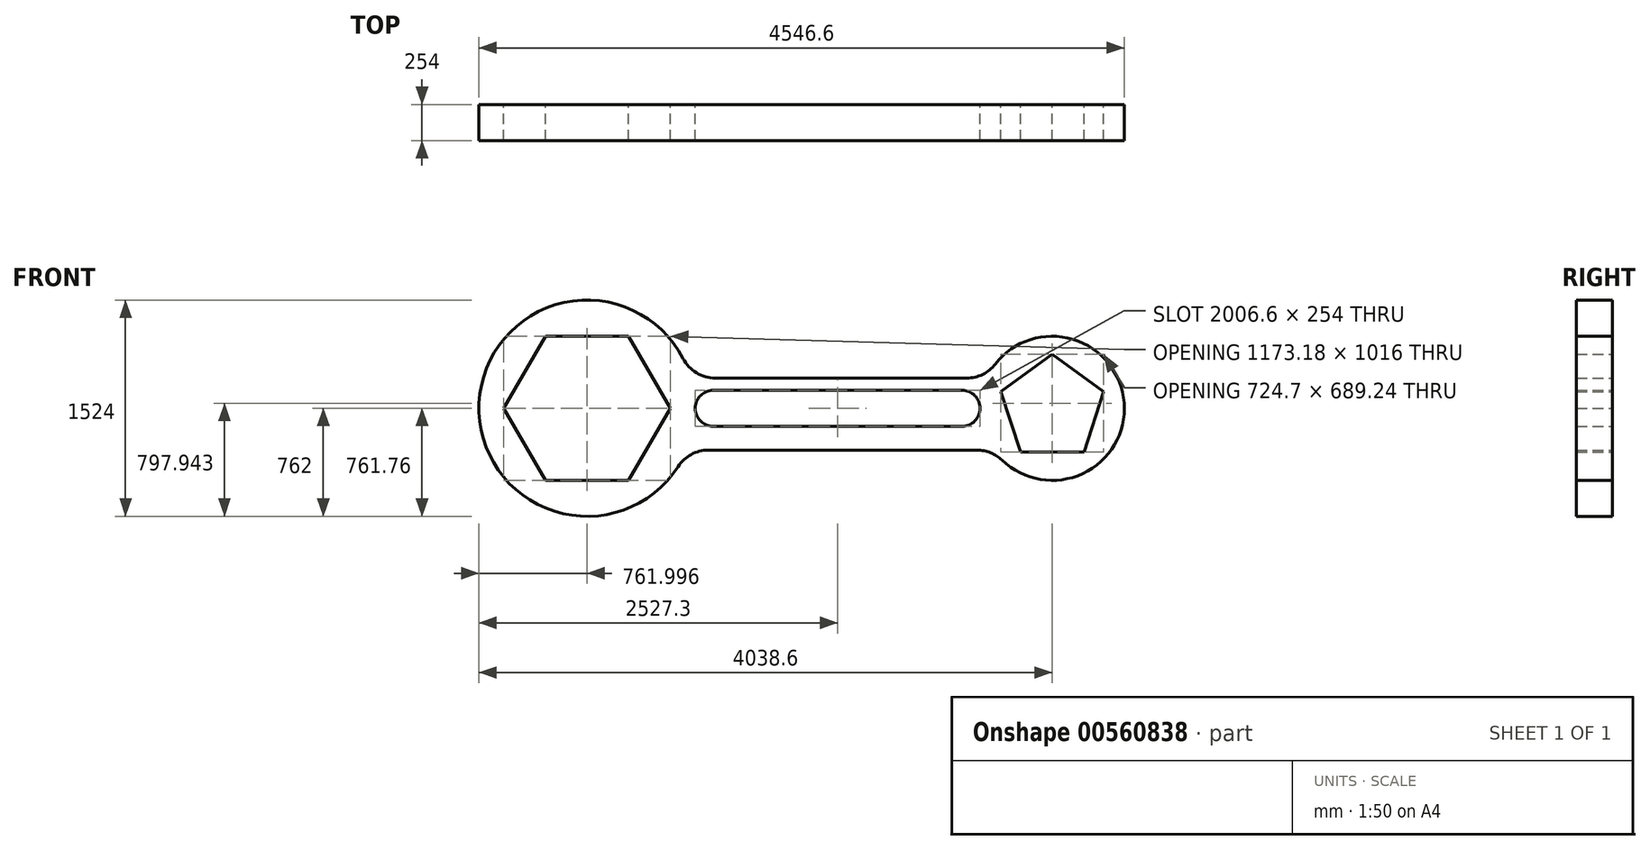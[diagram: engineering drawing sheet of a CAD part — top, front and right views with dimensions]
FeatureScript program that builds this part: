
annotation { "Feature Type Name" : "Feature", "Feature Type Description" : "" }
export const myFeature = defineFeature(function(context is Context, id is Id, definition is map)
    precondition{}
    {
        {
            var Q0;
            Q0=qCreatedBy(makeId("Front.planeOp"),FACE);
            var sketch = newSketch(context, id + "F0", { "sketchPlane" : qUnion([Q0])});
            skCircle(sketch, "E0", {"center": v(-12036.62, 0) * mm, "radius": 762 * mm});
            skCircle(sketch, "E1", {"center": v(-8760.02, -0.44) * mm, "radius": 508 * mm});
            skLineSegment(sketch, "E2", {"start": v(-11173.02, -127.24) * mm, "end": v(-9395.02, -127.24) * mm});
            skLineSegment(sketch, "E3", {"start": v(-11128.32, -250.7) * mm, "end": v(-11128.32, -250.7) * mm});
            skLineSegment(sketch, "E4", {"start": v(-11134.13, 212.66) * mm, "end": v(-9362.08, 212.66) * mm});
            skLineSegment(sketch, "E5", {"start": v(-9288.56, -295.34) * mm, "end": v(-11181.94, -295.34) * mm});
            skCircle(sketch, "E6.cCircle", {"center": v(-12036.62, 0) * mm, "radius": 508 * mm, "construction": true});
            skLineSegment(sketch, "E6.0", {"start": v(-11743.33, 508) * mm, "end": v(-11450.04, 0) * mm});
            skLineSegment(sketch, "E6.1", {"start": v(-11450.04, 0) * mm, "end": v(-11743.33, -508) * mm});
            skLineSegment(sketch, "E6.2", {"start": v(-11743.33, -508) * mm, "end": v(-12329.92, -508) * mm});
            skLineSegment(sketch, "E6.3", {"start": v(-12329.92, -508) * mm, "end": v(-12623.21, 0) * mm});
            skLineSegment(sketch, "E6.4", {"start": v(-12623.21, 0) * mm, "end": v(-12329.92, 508) * mm});
            skLineSegment(sketch, "E6.5", {"start": v(-12329.92, 508) * mm, "end": v(-11743.33, 508) * mm});
            skPoint(sketch, "E6.0.midPoint", {"position": v(-11596.68, 254) * mm});
            skArc(sketch, "E7", {"start": v(-11147.62, 126.76) * mm, "mid": v(-11274.62, -0.24) * mm, "end": v(-11147.62, -127.24) * mm});
            skLineSegment(sketch, "E8", {"start": v(-11147.62, 126.76) * mm, "end": v(-9395.02, 126.76) * mm});
            skArc(sketch, "E9", {"start": v(-9395.02, -127.24) * mm, "mid": v(-9268.02, -0.24) * mm, "end": v(-9395.02, 126.76) * mm});
            skCircle(sketch, "E10.cCircle", {"center": v(-8760.02, -0.44) * mm, "radius": 308.24 * mm, "construction": true});
            skLineSegment(sketch, "E10.0", {"start": v(-8760.02, 380.56) * mm, "end": v(-8397.67, 117.3) * mm});
            skLineSegment(sketch, "E10.1", {"start": v(-8397.67, 117.3) * mm, "end": v(-8536.08, -308.67) * mm});
            skLineSegment(sketch, "E10.2", {"start": v(-8536.08, -308.67) * mm, "end": v(-8983.97, -308.67) * mm});
            skLineSegment(sketch, "E10.3", {"start": v(-8983.97, -308.67) * mm, "end": v(-9122.38, 117.3) * mm});
            skLineSegment(sketch, "E10.4", {"start": v(-9122.38, 117.3) * mm, "end": v(-8760.02, 380.56) * mm});
            skPoint(sketch, "E10.0.midPoint", {"position": v(-8578.85, 248.93) * mm});
            skArc(sketch, "E11", {"start": v(-11359.76, 350) * mm, "mid": v(-11266.2, 249.69) * mm, "end": v(-11134.13, 212.66) * mm});
            skArc(sketch, "E12", {"start": v(-11181.94, -295.34) * mm, "mid": v(-11303.67, -326.4) * mm, "end": v(-11395.61, -412) * mm});
            skArc(sketch, "E13", {"start": v(-9112.38, -366.38) * mm, "mid": v(-9193.58, -313.77) * mm, "end": v(-9288.56, -295.34) * mm});
            skArc(sketch, "E14", {"start": v(-9362.08, 212.66) * mm, "mid": v(-9250.34, 238.55) * mm, "end": v(-9161.4, 310.96) * mm});
            skSolve(sketch);
        }
        {
            var Q0;
            Q0=makeQuery(id+"F0.imprint","IMPRINT",FACE,{"disambiguationData":[TD([[makeQuery(id+"F0.imprint","IMPRINT",EDGE,{"derivedFrom":sQuery(id+"F0.wireOp",EDGE,"E4")}),-1.0]])]});
            var Q1;
            Q1=makeQuery(id+"F0.imprint","IMPRINT",FACE,{"disambiguationData":[TD([[makeQuery(id+"F0.imprint","IMPRINT",EDGE,{"derivedFrom":sQuery(id+"F0.wireOp",EDGE,"E6.0")}),1.0]])]});
            var Q2;
            Q2=makeQuery(id+"F0.imprint","IMPRINT",FACE,{"disambiguationData":[TD([[makeQuery(id+"F0.imprint","IMPRINT",EDGE,{"derivedFrom":sQuery(id+"F0.wireOp",EDGE,"E10.0")}),1.0]])]});
            var Q3;
            Q3=makeQuery(id+"F0.imprint","IMPRINT",FACE,{"disambiguationData":[TD([[makeQuery(id+"F0.imprint","IMPRINT",EDGE,{"derivedFrom":sQuery(id+"F0.wireOp",EDGE,"E5")}),-1.0]])]});
            extrude(context, id + "F1", {"entities" : qUnion([Q0, Q1, Q2, Q3]), "depth" : 254 * mm, "offsetDistance" : 25.4 * mm});
        }
    });
